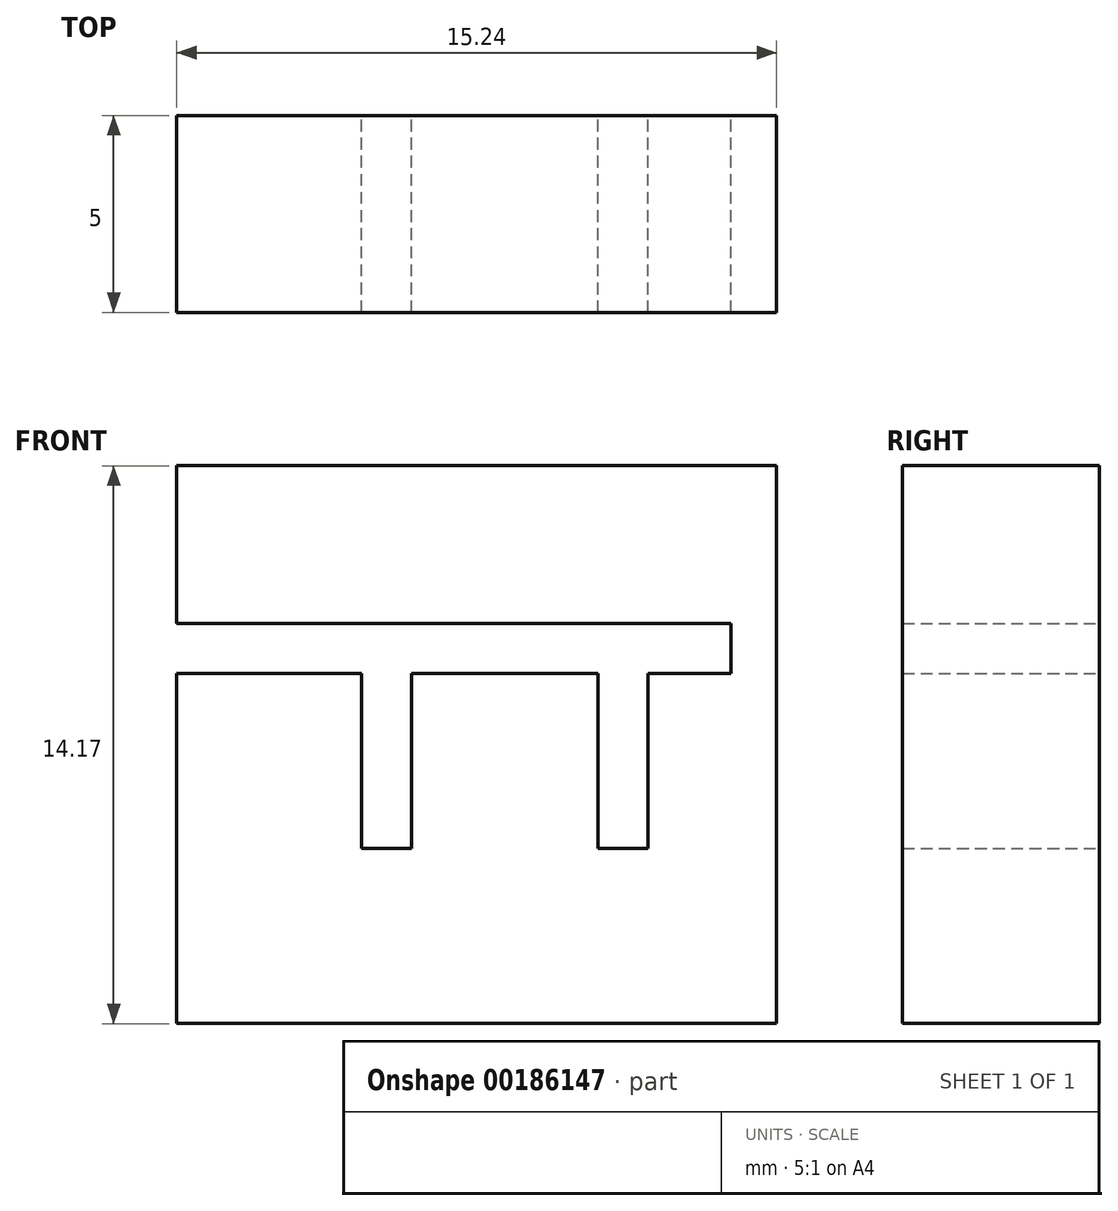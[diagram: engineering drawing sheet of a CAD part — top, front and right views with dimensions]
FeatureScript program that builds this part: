
annotation { "Feature Type Name" : "Feature", "Feature Type Description" : "" }
export const myFeature = defineFeature(function(context is Context, id is Id, definition is map)
    precondition{}
    {
        {
            var Q0;
            Q0=qCreatedBy(makeId("Front.planeOp"),FACE);
            var sketch = newSketch(context, id + "F0", { "sketchPlane" : qUnion([Q0])});
            skLineSegment(sketch, "E0.bottom", {"start": v(7.62, -4.44) * mm, "end": v(-7.62, -4.44) * mm});
            skLineSegment(sketch, "E0.top", {"start": v(6.45, 4.45) * mm, "end": v(4.34, 4.45) * mm});
            skLineSegment(sketch, "E0.left", {"start": v(7.62, -4.44) * mm, "end": v(7.62, 4.45) * mm});
            skLineSegment(sketch, "E0.right", {"start": v(-7.62, -4.45) * mm, "end": v(-7.62, 4.44) * mm});
            skPoint(sketch, "E0.middle", {"position": v(0, 0) * mm});
            skLineSegment(sketch, "E1.bottom", {"start": v(6.45, 5.72) * mm, "end": v(-7.62, 5.72) * mm});
            skLineSegment(sketch, "E1.top", {"start": v(7.62, 9.72) * mm, "end": v(-7.62, 9.72) * mm});
            skLineSegment(sketch, "E1.left", {"start": v(7.62, 5.71) * mm, "end": v(7.62, 9.72) * mm});
            skLineSegment(sketch, "E1.right", {"start": v(-7.62, 5.71) * mm, "end": v(-7.62, 9.72) * mm});
            skPoint(sketch, "E1.middle", {"position": v(0, 7.72) * mm});
            skLineSegment(sketch, "E2", {"start": v(6.45, 5.72) * mm, "end": v(6.45, 4.45) * mm});
            skLineSegment(sketch, "E3", {"start": v(7.62, 5.71) * mm, "end": v(7.62, 4.45) * mm});
            skLineSegment(sketch, "E4", {"start": v(-2.92, 4.45) * mm, "end": v(-2.92, 0) * mm});
            skLineSegment(sketch, "E5", {"start": v(-2.92, 0) * mm, "end": v(-1.65, 0) * mm});
            skLineSegment(sketch, "E6", {"start": v(-1.65, 0) * mm, "end": v(-1.65, 4.45) * mm});
            skLineSegment(sketch, "E7", {"start": v(-1.65, 4.45) * mm, "end": v(3.07, 4.45) * mm});
            skLineSegment(sketch, "E8", {"start": v(3.07, 4.45) * mm, "end": v(3.07, 0) * mm});
            skLineSegment(sketch, "E9", {"start": v(3.07, 0) * mm, "end": v(4.34, 0) * mm});
            skLineSegment(sketch, "E10", {"start": v(4.34, 0) * mm, "end": v(4.34, 4.45) * mm});
            skLineSegment(sketch, "E11.trimOffspring", {"start": v(3.07, 4.45) * mm, "end": v(-1.65, 4.45) * mm});
            skLineSegment(sketch, "E12.trimOffspring", {"start": v(-2.92, 4.45) * mm, "end": v(-7.62, 4.45) * mm});
            skSolve(sketch);
        }
        {
            var Q0;
            Q0=makeQuery(id+"F0.imprint","IMPRINT",FACE,{"disambiguationData":[TD([[makeQuery(id+"F0.imprint","IMPRINT",EDGE,{"derivedFrom":sQuery(id+"F0.wireOp",EDGE,"E0.bottom")}),-1.0]])]});
            extrude(context, id + "F1", {"entities" : qUnion([Q0]), "depth" : 5 * mm});
        }
    });
